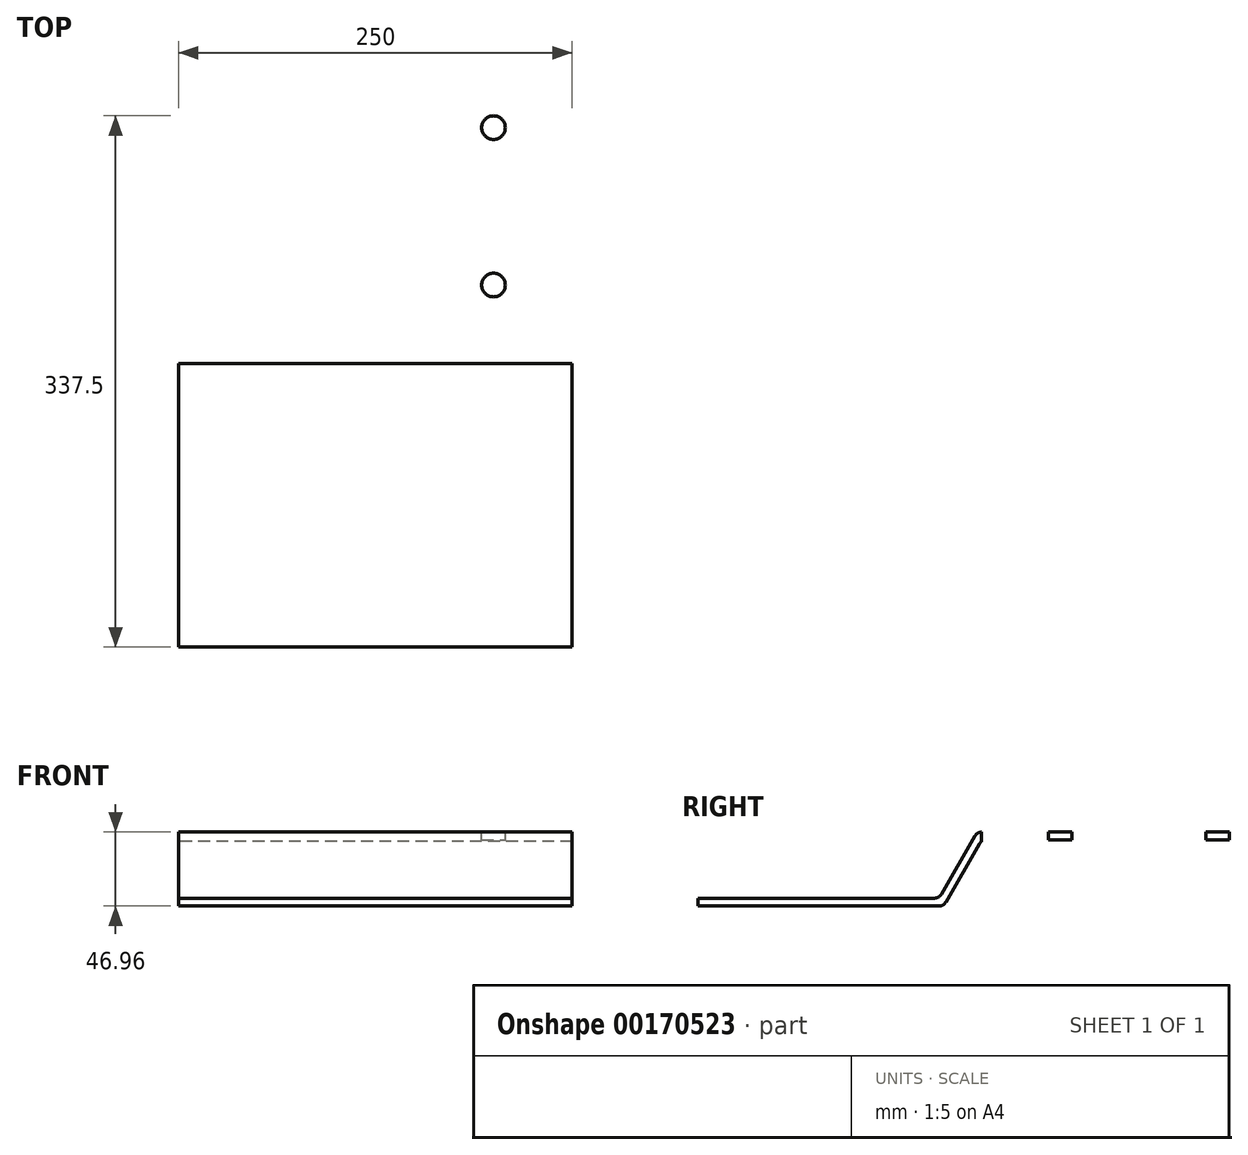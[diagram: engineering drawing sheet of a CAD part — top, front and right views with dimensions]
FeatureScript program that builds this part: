
annotation { "Feature Type Name" : "Feature", "Feature Type Description" : "" }
export const myFeature = defineFeature(function(context is Context, id is Id, definition is map)
    precondition{}
    {
        {
            var Q0;
            Q0=qCreatedBy(makeId("Right.planeOp"),FACE);
            var sketch = newSketch(context, id + "F0", { "sketchPlane" : qUnion([Q0])});
            skLineSegment(sketch, "E0.bottom", {"start": v(0, 0) * mm, "end": v(-197.11, 0) * mm});
            skLineSegment(sketch, "E0.top", {"start": v(0, 5) * mm, "end": v(-200, 5) * mm});
            skLineSegment(sketch, "E0.left", {"start": v(0, 0) * mm, "end": v(0, 5) * mm});
            skLineSegment(sketch, "E0.right", {"start": v(-200, 0) * mm, "end": v(-200, 5) * mm});
            skLineSegment(sketch, "E1", {"start": v(-201.44, -2.5) * mm, "end": v(-222.78, -39.46) * mm});
            skLineSegment(sketch, "E2", {"start": v(-227.11, -41.96) * mm, "end": v(-380, -41.96) * mm});
            skLineSegment(sketch, "E3", {"start": v(-380, -41.96) * mm, "end": v(-380, -36.96) * mm});
            skLineSegment(sketch, "E4.0", {"start": v(-204.33, 2.5) * mm, "end": v(-225.67, -34.46) * mm});
            skArc(sketch, "E5.filletArc", {"start": v(-200, 5) * mm, "mid": v(-202.5, 4.33) * mm, "end": v(-204.33, 2.5) * mm});
            skArc(sketch, "E6.filletArc", {"start": v(-197.11, 0) * mm, "mid": v(-199.61, -0.67) * mm, "end": v(-201.44, -2.5) * mm});
            skLineSegment(sketch, "E7", {"start": v(-380, -36.96) * mm, "end": v(-230, -36.96) * mm});
            skArc(sketch, "E8.filletArc", {"start": v(-230, -36.96) * mm, "mid": v(-227.5, -36.3) * mm, "end": v(-225.67, -34.46) * mm});
            skPoint(sketch, "E9.visualSharp", {"position": v(-224.23, -41.96) * mm});
            skArc(sketch, "E9.filletArc", {"start": v(-227.11, -41.96) * mm, "mid": v(-224.61, -41.3) * mm, "end": v(-222.78, -39.46) * mm});
            skSolve(sketch);
        }
        {
            var Q0;
            Q0=makeQuery(id+"F0.imprint","IMPRINT",FACE,{"disambiguationData":[TD([[makeQuery(id+"F0.imprint","IMPRINT",EDGE,{"derivedFrom":sQuery(id+"F0.wireOp",EDGE,"E0.bottom")}),-1.0]])]});
            extrude(context, id + "F1", {"entities" : qUnion([Q0]), "endBound" : BoundingType.SYMMETRIC, "depth" : 250 * mm});
        }
        {
            var Q0;
            Q0=makeQuery(id+"F1.opExtrude","SWEPT_FACE",FACE,{"disambiguationData":[OSD([sQuery(id+"F0.wireOp",EDGE,"E0.top")])]});
            var sketch = newSketch(context, id + "F2", { "sketchPlane" : qUnion([Q0])});
            skCircle(sketch, "E10", {"center": v(-75, -50) * mm, "radius": 7.5 * mm});
            skCircle(sketch, "E11", {"center": v(-75, -150) * mm, "radius": 7.5 * mm});
            skLineSegment(sketch, "E12", {"start": v(0, -394.28) * mm, "end": v(0, 43.1) * mm, "construction": true});
            skCircle(sketch, "E13.MirrorC", {"center": v(75, -50) * mm, "radius": 7.5 * mm});
            skCircle(sketch, "E14.MirrorC", {"center": v(75, -150) * mm, "radius": 7.5 * mm});
            skSolve(sketch);
        }
        {
            var Q0;
            Q0=makeQuery(id+"F2.imprint","IMPRINT",FACE,{"disambiguationData":[TD([[makeQuery(id+"F2.imprint","IMPRINT",EDGE,{"derivedFrom":sQuery(id+"F2.wireOp",EDGE,"E11")}),1.0]])]});
            var Q1;
            Q1=makeQuery(id+"F2.imprint","IMPRINT",FACE,{"disambiguationData":[TD([[makeQuery(id+"F2.imprint","IMPRINT",EDGE,{"derivedFrom":sQuery(id+"F2.wireOp",EDGE,"E14.MirrorC")}),-1.0]])]});
            var Q2;
            Q2=makeQuery(id+"F2.imprint","IMPRINT",FACE,{"disambiguationData":[TD([[makeQuery(id+"F2.imprint","IMPRINT",EDGE,{"derivedFrom":sQuery(id+"F2.wireOp",EDGE,"E13.MirrorC")}),-1.0]])]});
            var Q3;
            Q3=makeQuery(id+"F2.imprint","IMPRINT",FACE,{"disambiguationData":[TD([[makeQuery(id+"F2.imprint","IMPRINT",EDGE,{"derivedFrom":sQuery(id+"F2.wireOp",EDGE,"E10")}),1.0]])]});
            extrude(context, id + "F3", {"entities" : qUnion([Q0, Q1, Q2, Q3]), "operationType" : NewBodyOperationType.REMOVE, "endBound" : BoundingType.THROUGH_ALL, "oppositeDirection" : true, "depth" : 25 * mm});
        }
    });
